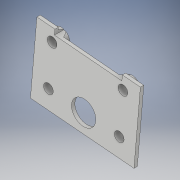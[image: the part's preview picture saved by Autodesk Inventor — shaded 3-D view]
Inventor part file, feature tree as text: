
AUTODESK INVENTOR PART (.ipt)
format: ipt  version: 2017 (Build 210142000, 142)  size: 1,982,976 bytes
history: native  units: in
note: dims shown in document units (in); Inventor stores cm internally (conversion verified against a paired STEP export)
features: extrude x6, sketch x6, projected_geometry x4, other x2, draft x1
ambient origin geometry x8: Origin, YZ Plane, XZ Plane, XY Plane, X Axis, Y Axis, Z Axis, Center Point
bodies: Solid1 (feature_tree)
feature tree (19):
  other  "ballSocket"
  other  "MeshFeature1"
  extrude  "Extrusion1"  Depth=0.2677in
  extrude  "Extrusion2"  TaperAngle=0.0deg  [1 undecoded]
  extrude  "Extrusion3"  TaperAngle=0.0deg  [1 undecoded]
  draft  "FaceDraft1"
  extrude  "Extrusion4"  TaperAngle=90.0deg  [1 undecoded]
  extrude  "Extrusion7"  Depth=0.1969in
  extrude  "Extrusion8"  Depth=0.7874in
  sketch  "Sketch1"  dims[d0=0.4528in d1=0.0in d2=0.2677in]
  sketch  "Sketch2"  dims[d3=0.3707in d4=0.0in]
  sketch  "Sketch3"  dims[d5=0.113in d6=0.0in]
  sketch  "Sketch4"  dims[d7=0.4079in d8=90.0deg]
  projected_geometry  "Projected Loop2"
  projected_geometry  "Projected Loop3"
  projected_geometry  "Projected Loop4"
  projected_geometry  "Projected Loop5"
  sketch  "Sketch7"  dims[d9=0.113in d10=0.1969in]
  sketch  "Sketch8"  dims[d11=0.1969in d13=0.0787in d14=0.0394in d15=0.0in d16=0.2677in d17=0.3569in d18=0.0in d19=0.113in d20=0.0in d22=0.113in d23=0.1969in d24=0.1969in d25=0.0787in d26=0.0669in d27=0.0in d28=0.1374in d29=0.1575in d30=0.0in d33=0.8268in d35=0.4921in d38=0.0866in d39=0.3937in d40=0.0344in d41=0.7874in d42=0.3937in d43=0.0in d44=0.5906in d45=0.0in]
note: 3 required parameter values undecoded (feature->parameter linkage not recoverable at this tier; creation-order binding heuristic only, values carry confidence <= 0.55)
